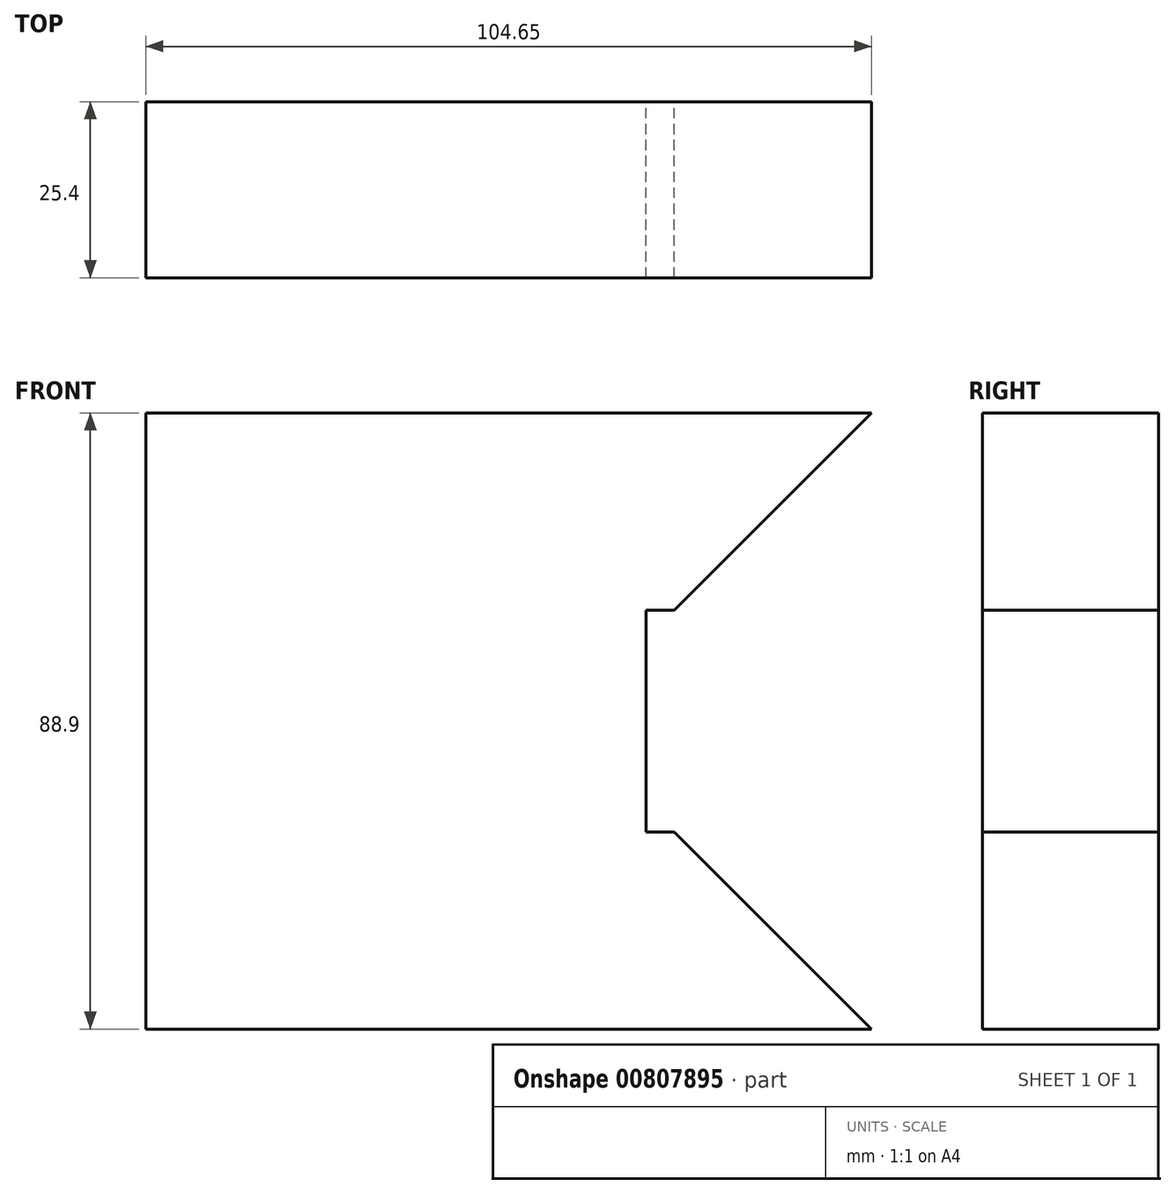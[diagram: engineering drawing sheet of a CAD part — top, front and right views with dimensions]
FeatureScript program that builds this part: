
annotation { "Feature Type Name" : "Feature", "Feature Type Description" : "" }
export const myFeature = defineFeature(function(context is Context, id is Id, definition is map)
    precondition{}
    {
        {
            var Q0;
            Q0=qCreatedBy(makeId("Front.planeOp"),FACE);
            var sketch = newSketch(context, id + "F0", { "sketchPlane" : qUnion([Q0])});
            skLineSegment(sketch, "E0", {"start": v(-48.94, -28.45) * mm, "end": v(55.7, -28.45) * mm});
            skLineSegment(sketch, "E1", {"start": v(-48.94, -28.45) * mm, "end": v(-48.94, 0) * mm});
            skLineSegment(sketch, "E2", {"start": v(-48.94, 0) * mm, "end": v(-48.94, 16) * mm});
            skLineSegment(sketch, "E3", {"start": v(-48.94, 0) * mm, "end": v(27.26, 0) * mm});
            skLineSegment(sketch, "E4", {"start": v(55.7, -28.45) * mm, "end": v(27.26, 0) * mm});
            skLineSegment(sketch, "E5", {"start": v(-48.94, 16) * mm, "end": v(23.22, 16) * mm});
            skLineSegment(sketch, "E6", {"start": v(23.22, 16) * mm, "end": v(23.22, 0) * mm});
            skSolve(sketch);
        }
        {
            var Q0;
            Q0=makeQuery(id+"F0.imprint","IMPRINT",FACE,{"disambiguationData":[TD([[makeQuery(id+"F0.imprint","IMPRINT",EDGE,{"derivedFrom":sQuery(id+"F0.wireOp",EDGE,"E0")}),1.0]])]});
            var Q1;
            {var subQ0=sQuery(id+"F0.wireOp",EDGE,"E2");Q1=makeQuery(id+"F0.imprint","IMPRINT",FACE,{"disambiguationData":[TD([[makeQuery(id+"F0.imprint","IMPRINT",EDGE,{"derivedFrom":subQ0}),-1.0]])]});}
            extrude(context, id + "F1", {"entities" : qUnion([Q0, Q1]), "depth" : 25.4 * mm, "offsetDistance" : 25.4 * mm});
        }
        {
            var Q0;
            Q0=makeQuery(id+"F1.opExtrude","SWEPT_BODY",BODY,{"disambiguationData":[OSD([sQuery(id+"F0.wireOp",EDGE,"E0"),sQuery(id+"F0.wireOp",EDGE,"E1"),sQuery(id+"F0.wireOp",EDGE,"E2"),sQuery(id+"F0.wireOp",EDGE,"E3"),sQuery(id+"F0.wireOp",EDGE,"E4"),sQuery(id+"F0.wireOp",EDGE,"E5"),sQuery(id+"F0.wireOp",EDGE,"E6")])]});
            var Q1;
            Q1=makeQuery(id+"F1.opExtrude","SWEPT_FACE",FACE,{"disambiguationData":[OSD([sQuery(id+"F0.wireOp",EDGE,"E5")])]});
            mirror(context, id + "F2", {"operationType" : NewBodyOperationType.ADD, "entities" : qUnion([Q0]), "mirrorPlane" : qUnion([Q1])});
        }
    });
